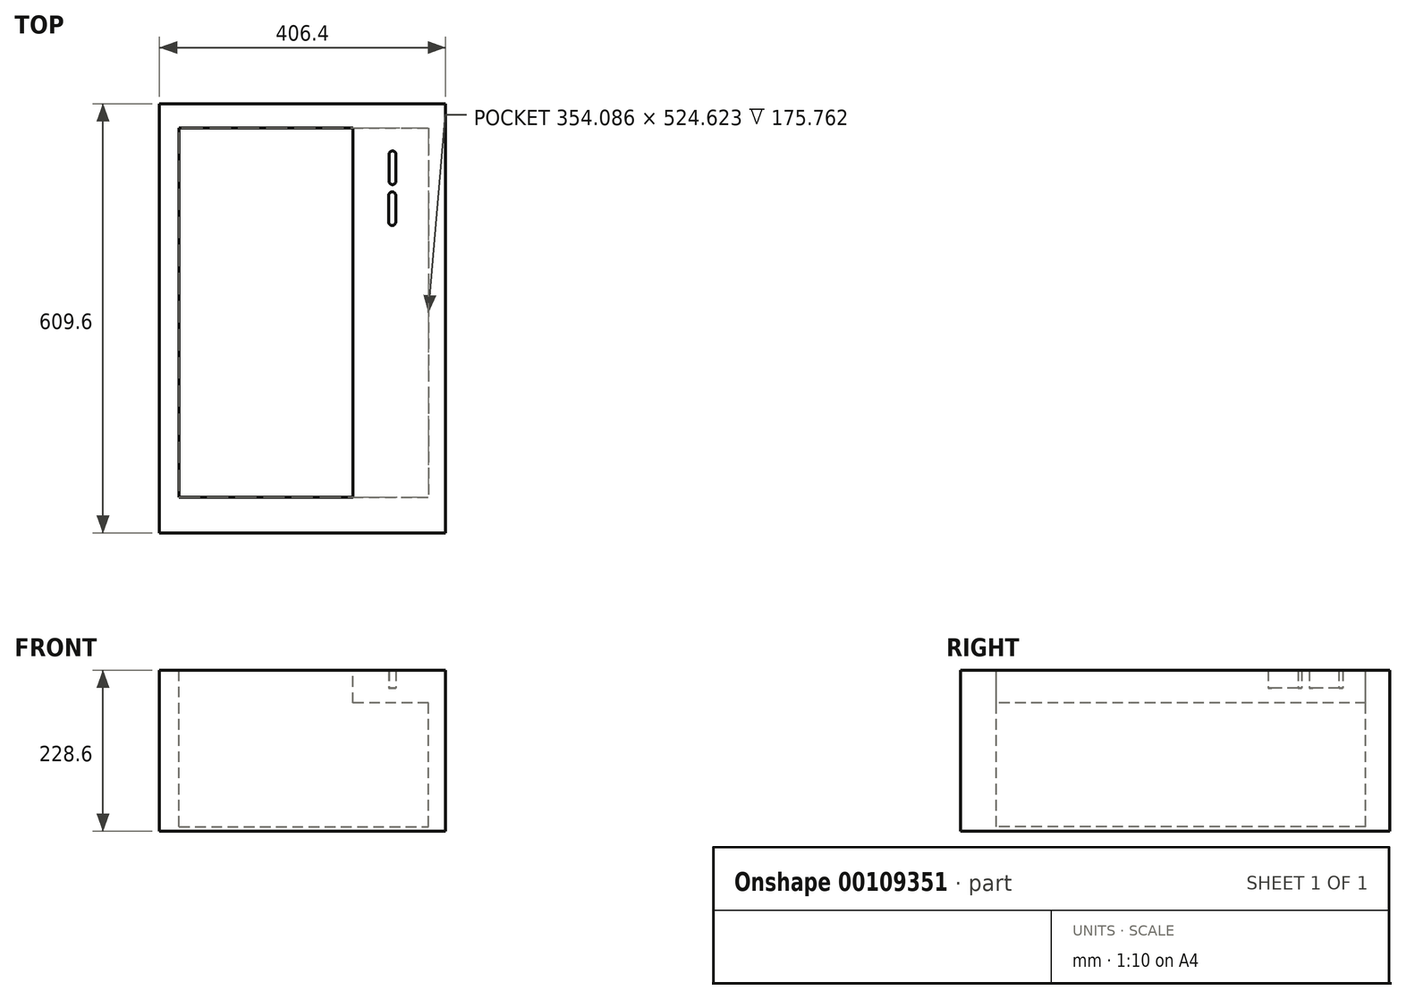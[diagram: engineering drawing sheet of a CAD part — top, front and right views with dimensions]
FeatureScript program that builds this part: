
annotation { "Feature Type Name" : "Feature", "Feature Type Description" : "" }
export const myFeature = defineFeature(function(context is Context, id is Id, definition is map)
    precondition{}
    {
        {
            var Q0;
            Q0=qCreatedBy(makeId("Top.planeOp"),FACE);
            var sketch = newSketch(context, id + "F0", { "sketchPlane" : qUnion([Q0])});
            skLineSegment(sketch, "E0.bottom", {"start": v(203.2, -304.8) * mm, "end": v(-203.2, -304.8) * mm});
            skLineSegment(sketch, "E0.top", {"start": v(203.2, 304.8) * mm, "end": v(-203.2, 304.8) * mm});
            skLineSegment(sketch, "E0.left", {"start": v(203.2, -304.8) * mm, "end": v(203.2, 304.8) * mm});
            skLineSegment(sketch, "E0.right", {"start": v(-203.2, -304.8) * mm, "end": v(-203.2, 304.8) * mm});
            skPoint(sketch, "E0.middle", {"position": v(0, 0) * mm});
            skSolve(sketch);
        }
        {
            var Q0;
            Q0=makeQuery(id+"F0.imprint","IMPRINT",FACE,{"disambiguationData":[TD([[makeQuery(id+"F0.imprint","IMPRINT",EDGE,{"derivedFrom":sQuery(id+"F0.wireOp",EDGE,"E0.bottom")}),-1.0]])]});
            extrude(context, id + "F1", {"entities" : qUnion([Q0]), "depth" : 203.2 * mm});
        }
        {
            var Q0;
            Q0=makeQuery(id+"F1.opExtrude","CAP_FACE",FACE,{"disambiguationData":[OSD([sQuery(id+"F0.wireOp",EDGE,"E0.bottom"),sQuery(id+"F0.wireOp",EDGE,"E0.top"),sQuery(id+"F0.wireOp",EDGE,"E0.left"),sQuery(id+"F0.wireOp",EDGE,"E0.right")])],"isStart":false});
            var sketch = newSketch(context, id + "F2", { "sketchPlane" : qUnion([Q0])});
            skLineSegment(sketch, "E1.bottom", {"start": v(-175.27, 270.6) * mm, "end": v(71.32, 270.6) * mm});
            skLineSegment(sketch, "E1.top", {"start": v(-175.27, -254.01) * mm, "end": v(71.32, -254.01) * mm});
            skLineSegment(sketch, "E1.left", {"start": v(-175.27, 270.6) * mm, "end": v(-175.27, -254.01) * mm});
            skLineSegment(sketch, "E1.right", {"start": v(71.32, 270.6) * mm, "end": v(71.32, -254.01) * mm});
            skSolve(sketch);
        }
        {
            var Q0;
            Q0=makeQuery(id+"F2.imprint","IMPRINT",FACE,{"disambiguationData":[TD([[makeQuery(id+"F2.imprint","IMPRINT",EDGE,{"derivedFrom":sQuery(id+"F2.wireOp",EDGE,"E1.bottom")}),-1.0]])]});
            extrude(context, id + "F3", {"entities" : qUnion([Q0]), "operationType" : NewBodyOperationType.REMOVE, "oppositeDirection" : true, "depth" : 196.85 * mm});
        }
        {
            var Q0;
            Q0=makeQuery(id+"F3.boolean.opBoolean","COPY",FACE,{"derivedFrom":makeQuery(id+"F3.opExtrude","SWEPT_FACE",FACE,{"disambiguationData":[OSD([sQuery(id+"F2.wireOp",EDGE,"E1.right")])]})});
            var sketch = newSketch(context, id + "F4", { "sketchPlane" : qUnion([Q0])});
            skLineSegment(sketch, "E2", {"start": v(-270.6, 182.11) * mm, "end": v(254.01, 182.11) * mm});
            skSolve(sketch);
        }
        {
            var Q0;
            {var subQ0=sQuery(id+"F4.wireOp",EDGE,"E2");Q0=makeQuery(id+"F4.imprint","IMPRINT",FACE,{"disambiguationData":[TD([[makeQuery(id+"F4.imprint","IMPRINT",EDGE,{"derivedFrom":subQ0}),-1.0]])]});}
            extrude(context, id + "F5", {"entities" : qUnion([Q0]), "operationType" : NewBodyOperationType.REMOVE, "oppositeDirection" : true, "depth" : 107.49 * mm});
        }
        {
            var Q0;
            Q0=makeQuery(id+"F1.opExtrude","CAP_FACE",FACE,{"disambiguationData":[OSD([sQuery(id+"F0.wireOp",EDGE,"E0.bottom"),sQuery(id+"F0.wireOp",EDGE,"E0.top"),sQuery(id+"F0.wireOp",EDGE,"E0.left"),sQuery(id+"F0.wireOp",EDGE,"E0.right")])],"isStart":false});
            var sketch = newSketch(context, id + "F6", { "sketchPlane" : qUnion([Q0])});
            skArc(sketch, "E3", {"start": v(132.83, 232.87) * mm, "mid": v(127.6, 237.85) * mm, "end": v(122.88, 232.4) * mm});
            skArc(sketch, "E4", {"start": v(122.86, 195.1) * mm, "mid": v(127.84, 190.12) * mm, "end": v(132.82, 195.1) * mm});
            skLineSegment(sketch, "E5", {"start": v(132.83, 232.87) * mm, "end": v(132.82, 195.1) * mm});
            skLineSegment(sketch, "E6", {"start": v(122.88, 232.4) * mm, "end": v(122.86, 195.1) * mm});
            skArc(sketch, "E7", {"start": v(132.4, 174.69) * mm, "mid": v(127.18, 179.67) * mm, "end": v(122.45, 174.22) * mm});
            skArc(sketch, "E8", {"start": v(122.43, 136.92) * mm, "mid": v(127.41, 131.94) * mm, "end": v(132.4, 136.92) * mm});
            skLineSegment(sketch, "E9", {"start": v(132.4, 174.7) * mm, "end": v(132.4, 136.92) * mm});
            skLineSegment(sketch, "E10", {"start": v(122.45, 174.22) * mm, "end": v(122.43, 136.92) * mm});
            skSolve(sketch);
        }
        {
            var Q0;
            {var subQ4=sQuery(id+"F6.wireOp",EDGE,"E3");Q0=makeQuery(id+"F6.imprint","IMPRINT",FACE,{"disambiguationData":[TD([[makeQuery(id+"F6.imprint","IMPRINT",EDGE,{"derivedFrom":subQ4}),-1.0]])]});}
            extrude(context, id + "F7", {"entities" : qUnion([Q0]), "operationType" : NewBodyOperationType.ADD, "depth" : 25.4 * mm});
        }
    });
